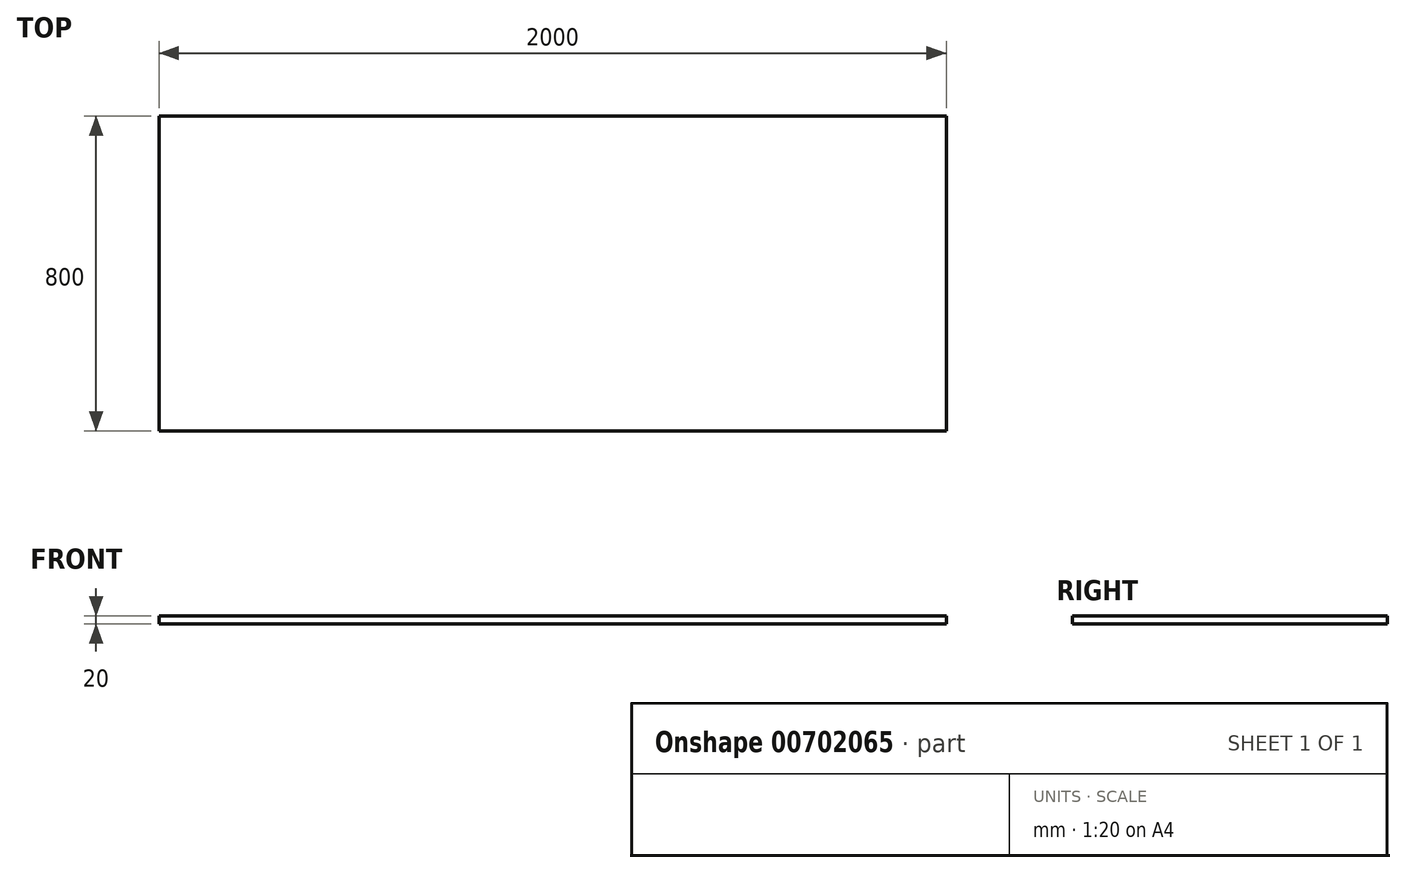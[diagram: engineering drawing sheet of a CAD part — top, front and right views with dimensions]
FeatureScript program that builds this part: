
annotation { "Feature Type Name" : "Feature", "Feature Type Description" : "" }
export const myFeature = defineFeature(function(context is Context, id is Id, definition is map)
    precondition{}
    {
        {
            var Q0;
            Q0=qCreatedBy(makeId("Top.planeOp"),FACE);
            var sketch = newSketch(context, id + "F0", { "sketchPlane" : qUnion([Q0])});
            skLineSegment(sketch, "E0.bottom", {"start": v(1000, 400) * mm, "end": v(-1000, 400) * mm});
            skLineSegment(sketch, "E0.top", {"start": v(1000, -400) * mm, "end": v(-1000, -400) * mm});
            skLineSegment(sketch, "E0.left", {"start": v(1000, 400) * mm, "end": v(1000, -400) * mm});
            skLineSegment(sketch, "E0.right", {"start": v(-1000, 400) * mm, "end": v(-1000, -400) * mm});
            skPoint(sketch, "E0.middle", {"position": v(0, 0) * mm});
            skSolve(sketch);
        }
        {
            var Q0;
            Q0 = qSketchRegion(id + "F0", true);
            extrude(context, id + "F1", {"entities" : qUnion([Q0]), "depth" : 20 * mm, "offsetDistance" : 25 * mm});
        }
    });
